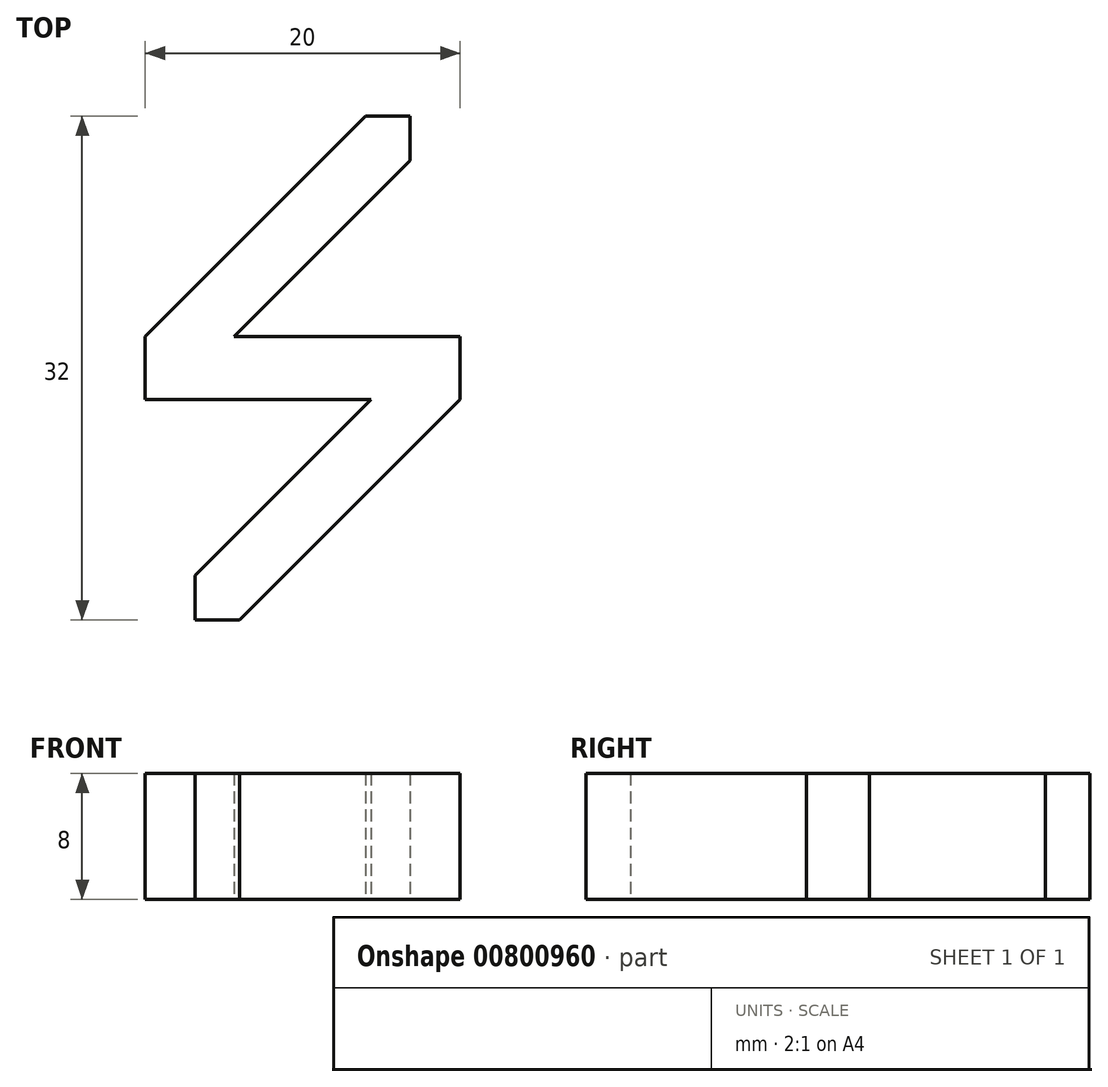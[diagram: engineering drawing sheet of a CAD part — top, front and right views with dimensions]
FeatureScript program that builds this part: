
annotation { "Feature Type Name" : "Feature", "Feature Type Description" : "" }
export const myFeature = defineFeature(function(context is Context, id is Id, definition is map)
    precondition{}
    {
        {
            var Q0;
            Q0=qCreatedBy(makeId("Top.planeOp"),FACE);
            var sketch = newSketch(context, id + "F0", { "sketchPlane" : qUnion([Q0])});
            skLineSegment(sketch, "E0", {"start": v(16.83, 0) * mm, "end": v(14, 0) * mm});
            skLineSegment(sketch, "E1", {"start": v(14, 0) * mm, "end": v(0, -14) * mm});
            skLineSegment(sketch, "E2", {"start": v(0, -14) * mm, "end": v(0, -18) * mm});
            skLineSegment(sketch, "E3", {"start": v(0, -18) * mm, "end": v(14.34, -18) * mm});
            skLineSegment(sketch, "E4", {"start": v(20, -14) * mm, "end": v(5.66, -14) * mm});
            skLineSegment(sketch, "E5", {"start": v(5.66, -14) * mm, "end": v(16.83, -2.83) * mm});
            skLineSegment(sketch, "E6", {"start": v(16.83, -2.83) * mm, "end": v(16.83, 0) * mm});
            skLineSegment(sketch, "E7", {"start": v(6, -32) * mm, "end": v(20, -18) * mm});
            skLineSegment(sketch, "E8", {"start": v(20, -18) * mm, "end": v(20, -14) * mm});
            skLineSegment(sketch, "E9", {"start": v(14.34, -18) * mm, "end": v(20, -18) * mm, "construction": true});
            skLineSegment(sketch, "E10", {"start": v(6, -32) * mm, "end": v(3.17, -32) * mm});
            skLineSegment(sketch, "E11", {"start": v(3.17, -32) * mm, "end": v(3.17, -29.17) * mm});
            skLineSegment(sketch, "E12", {"start": v(3.17, -29.17) * mm, "end": v(14.34, -18) * mm});
            skSolve(sketch);
        }
        {
            var Q0;
            Q0=makeQuery(id+"F0.imprint","IMPRINT",FACE,{"disambiguationData":[TD([[makeQuery(id+"F0.imprint","IMPRINT",EDGE,{"derivedFrom":sQuery(id+"F0.wireOp",EDGE,"E0")}),1.0]])]});
            extrude(context, id + "F1", {"entities" : qUnion([Q0]), "depth" : 8 * mm, "offsetDistance" : 25 * mm});
        }
    });
